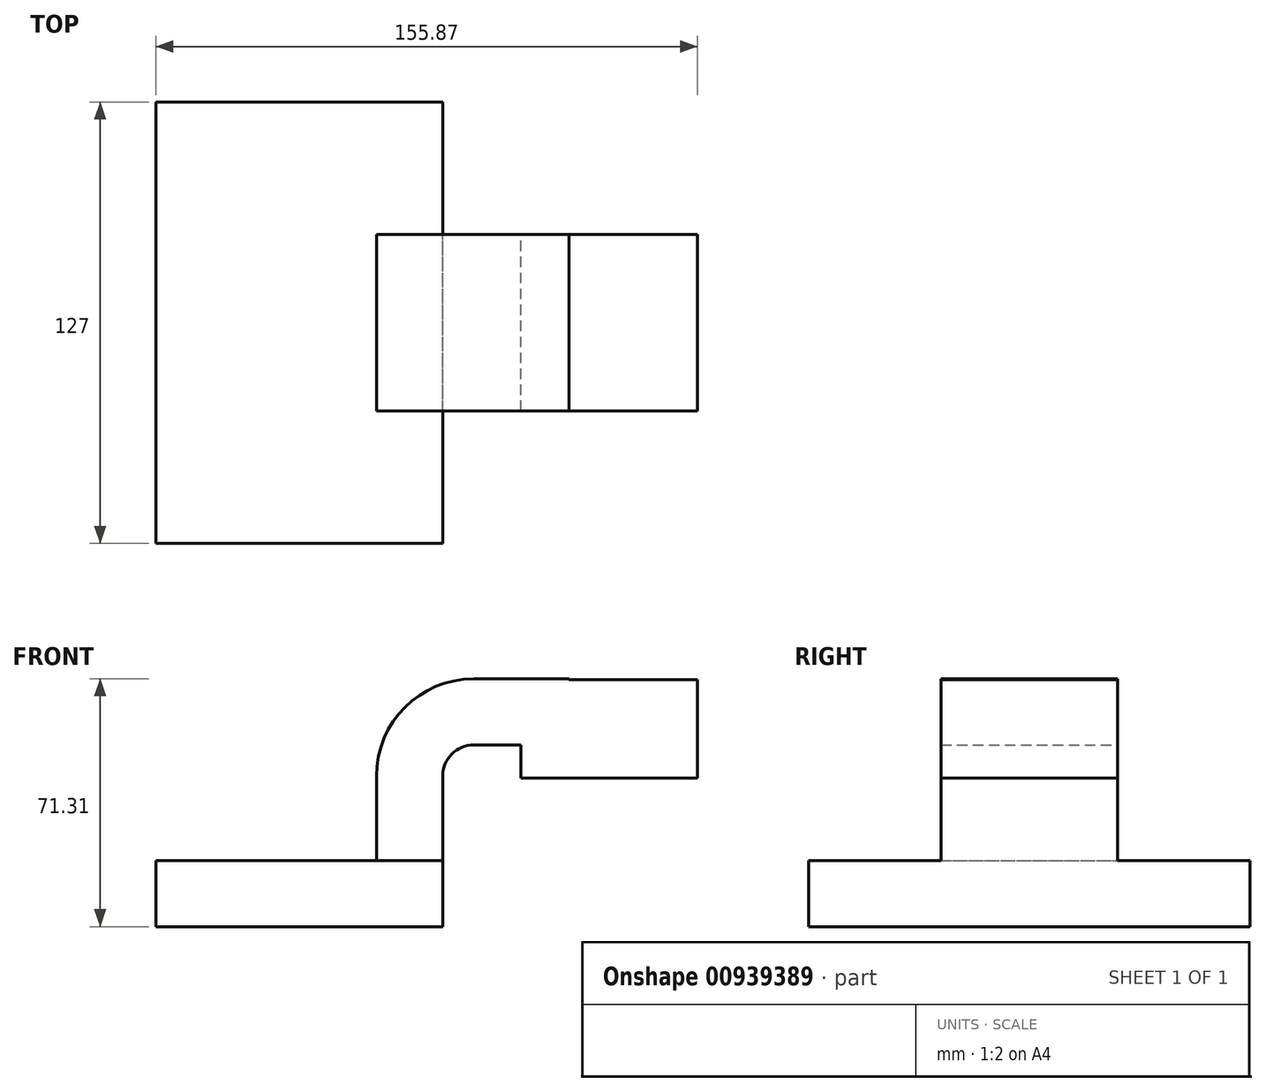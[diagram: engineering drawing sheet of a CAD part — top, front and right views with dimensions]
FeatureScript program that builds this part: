
annotation { "Feature Type Name" : "Feature", "Feature Type Description" : "" }
export const myFeature = defineFeature(function(context is Context, id is Id, definition is map)
    precondition{}
    {
        {
            var Q0;
            Q0=qCreatedBy(makeId("Front.planeOp"),FACE);
            var sketch = newSketch(context, id + "F0", { "sketchPlane" : qUnion([Q0])});
            skLineSegment(sketch, "E0.bottom", {"start": v(-41.28, -9.53) * mm, "end": v(41.28, -9.53) * mm});
            skLineSegment(sketch, "E0.top", {"start": v(-41.28, 9.53) * mm, "end": v(41.28, 9.53) * mm});
            skLineSegment(sketch, "E0.left", {"start": v(-41.28, -9.53) * mm, "end": v(-41.28, 9.53) * mm});
            skLineSegment(sketch, "E0.right", {"start": v(41.28, -9.53) * mm, "end": v(41.28, 9.52) * mm});
            skPoint(sketch, "E0.middle", {"position": v(0, 0) * mm});
            skLineSegment(sketch, "E1.bottom", {"start": v(114.59, 33.21) * mm, "end": v(63.79, 33.21) * mm});
            skLineSegment(sketch, "E1.top", {"start": v(114.59, 61.57) * mm, "end": v(63.79, 61.57) * mm});
            skLineSegment(sketch, "E1.left", {"start": v(114.59, 33.21) * mm, "end": v(114.59, 61.57) * mm});
            skLineSegment(sketch, "E1.right", {"start": v(63.79, 33.21) * mm, "end": v(63.79, 61.57) * mm});
            skPoint(sketch, "E1.middle", {"position": v(89.19, 47.39) * mm});
            skLineSegment(sketch, "E2", {"start": v(41.28, 9.52) * mm, "end": v(41.28, 33.83) * mm});
            skArc(sketch, "E3", {"start": v(41.28, 33.83) * mm, "mid": v(43.88, 40.13) * mm, "end": v(50.17, 42.73) * mm});
            skLineSegment(sketch, "E4", {"start": v(50.17, 42.73) * mm, "end": v(77.69, 42.73) * mm});
            skLineSegment(sketch, "E5.0", {"start": v(50.17, 61.78) * mm, "end": v(77.69, 61.78) * mm});
            skArc(sketch, "E5.1", {"start": v(22.23, 33.83) * mm, "mid": v(30.41, 53.6) * mm, "end": v(50.17, 61.78) * mm});
            skLineSegment(sketch, "E5.2", {"start": v(22.22, 9.52) * mm, "end": v(22.22, 33.83) * mm});
            skLineSegment(sketch, "E6", {"start": v(77.84, 33.21) * mm, "end": v(77.69, 61.78) * mm});
            skFitSpline(sketch, "E7", {"points": [v(-41.28, 9.52) * mm, v(50.17, 61.78) * mm], "startDerivative": vector(13.28, 108.12) * mm, "endDerivative": vector(128.61, -1.42) * mm});
            skSolve(sketch);
        }
        {
            var Q0;
            Q0=makeQuery(id+"F0.imprint","IMPRINT",FACE,{"disambiguationData":[TD([[makeQuery(id+"F0.imprint","IMPRINT",EDGE,{"derivedFrom":sQuery(id+"F0.wireOp",EDGE,"E0.bottom")}),1.0]])]});
            extrude(context, id + "F1", {"entities" : qUnion([Q0]), "endBound" : BoundingType.SYMMETRIC, "depth" : 127 * mm, "offsetDistance" : 25.4 * mm});
        }
        {
            var Q0;
            {var subQ8=sQuery(id+"F0.wireOp",EDGE,"E2");Q0=makeQuery(id+"F0.imprint","IMPRINT",FACE,{"disambiguationData":[TD([[makeQuery(id+"F0.imprint","IMPRINT",EDGE,{"derivedFrom":subQ8}),1.0]])]});}
            extrude(context, id + "F2", {"entities" : qUnion([Q0]), "operationType" : NewBodyOperationType.ADD, "endBound" : BoundingType.SYMMETRIC, "depth" : 50.8 * mm, "offsetDistance" : 25.4 * mm});
        }
        {
            var Q0;
            Q0=makeQuery(id+"F0.imprint","IMPRINT",FACE,{"disambiguationData":[TD([[makeQuery(id+"F0.imprint","IMPRINT",EDGE,{"derivedFrom":sQuery(id+"F0.wireOp",EDGE,"E5.1")}),1.0]])]});
            extrude(context, id + "F3", {"entities" : qUnion([Q0]), "operationType" : NewBodyOperationType.ADD, "endBound" : BoundingType.SYMMETRIC, "depth" : 15.88 * mm, "offsetDistance" : 25.4 * mm});
        }
        {
            var Q0;
            {var subQ0=sQuery(id+"F0.wireOp",EDGE,"E1.left");Q0=makeQuery(id+"F0.imprint","IMPRINT",FACE,{"disambiguationData":[TD([[makeQuery(id+"F0.imprint","IMPRINT",EDGE,{"derivedFrom":subQ0}),1.0]])]});}
            var Q1;
            {var subQ0=sQuery(id+"F0.wireOp",EDGE,"E1.right");var subQ1=sQuery(id+"F0.wireOp",EDGE,"E1.bottom");var subQ2=makeQuery(id+"F0.imprint","INTERSECT",VERTEX,{"derivedFrom":[subQ1,subQ0]});Q1=makeQuery(id+"F0.imprint","IMPRINT",FACE,{"disambiguationData":[TD([[makeQuery(id+"F0.imprint","IMPRINT",EDGE,{"disambiguationData":[TD([[subQ2,1.0]])],"derivedFrom":subQ1}),-1.0]])]});}
            extrude(context, id + "F4", {"entities" : qUnion([Q0, Q1]), "operationType" : NewBodyOperationType.ADD, "endBound" : BoundingType.SYMMETRIC, "depth" : 50.8 * mm, "offsetDistance" : 25.4 * mm});
        }
    });
